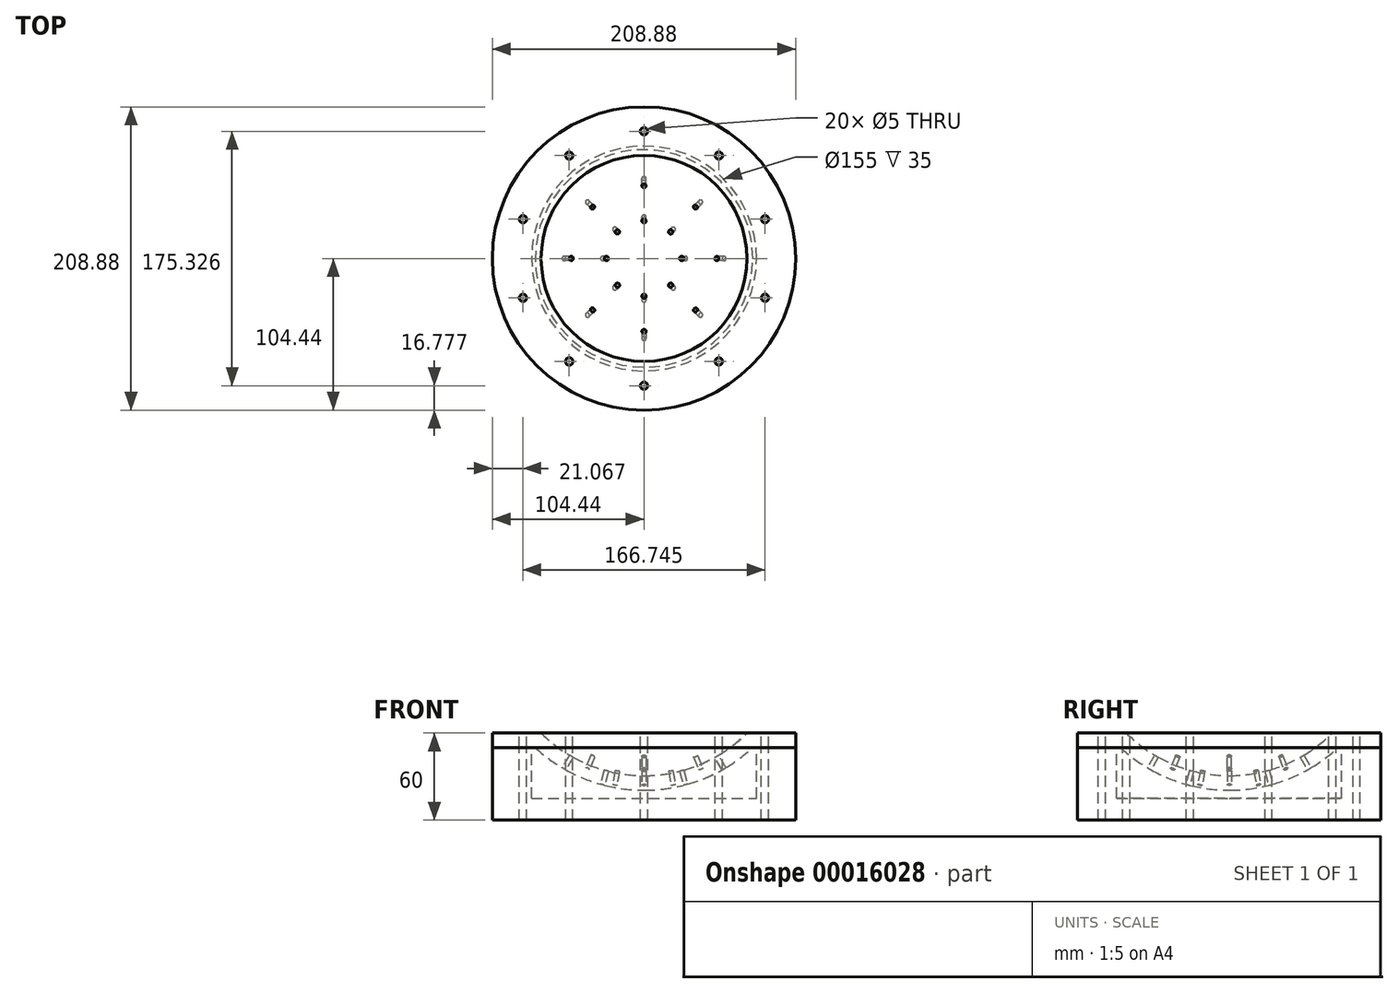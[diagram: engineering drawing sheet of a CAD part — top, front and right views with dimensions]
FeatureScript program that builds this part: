
annotation { "Feature Type Name" : "Feature", "Feature Type Description" : "" }
export const myFeature = defineFeature(function(context is Context, id is Id, definition is map)
    precondition{}
    {
        {
            var Q0;
            Q0=qCreatedBy(makeId("Front.planeOp"),FACE);
            var sketch = newSketch(context, id + "F0", { "sketchPlane" : qUnion([Q0])});
            skArc(sketch, "E0", {"start": v(0, -100.25) * mm, "mid": v(38.36, -92.62) * mm, "end": v(70.89, -70.89) * mm});
            skArc(sketch, "E1", {"start": v(0, -110.25) * mm, "mid": v(40.23, -102.65) * mm, "end": v(74.92, -80.89) * mm});
            skLineSegment(sketch, "E2", {"start": v(0, -100.25) * mm, "end": v(0, -110.25) * mm});
            skLineSegment(sketch, "E3", {"start": v(70.89, -70.89) * mm, "end": v(84.44, -70.89) * mm});
            skLineSegment(sketch, "E4", {"start": v(84.44, -70.89) * mm, "end": v(104.44, -70.89) * mm});
            skLineSegment(sketch, "E5", {"start": v(104.44, -70.89) * mm, "end": v(104.44, -80.89) * mm});
            skLineSegment(sketch, "E6", {"start": v(104.44, -80.89) * mm, "end": v(74.92, -80.89) * mm});
            skLineSegment(sketch, "E7", {"start": v(0, 0) * mm, "end": v(0, -110.25) * mm, "construction": true});
            skLineSegment(sketch, "E8", {"start": v(0, 0) * mm, "end": v(50.13, -86.82) * mm, "construction": true});
            skLineSegment(sketch, "E9", {"start": v(0, 0) * mm, "end": v(25.95, -96.83) * mm, "construction": true});
            skSolve(sketch);
        }
        {
            var Q0;
            Q0=makeQuery(id+"F0.imprint","IMPRINT",FACE,{"disambiguationData":[TD([[makeQuery(id+"F0.imprint","IMPRINT",EDGE,{"derivedFrom":sQuery(id+"F0.wireOp",EDGE,"E0")}),-1.0]])]});
            var Q1;
            Q1=sQuery(id+"F0.wireOp",EDGE,"E7");
            revolve(context, id + "F1", {"entities" : qUnion([Q0]), "axis" : qUnion([Q1]), "revolveType" : RevolveType.FULL});
        }
        {
            var Q0;
            Q0=makeQuery(id+"F1.opRevolve","SWEPT_FACE",FACE,{"disambiguationData":[OSD([sQuery(id+"F0.wireOp",EDGE,"E3"),sQuery(id+"F0.wireOp",EDGE,"E4")])]});
            var sketch = newSketch(context, id + "F2", { "sketchPlane" : qUnion([Q0])});
            skCircle(sketch, "E10", {"center": v(0, 87.66) * mm, "radius": 2.5 * mm});
            skCircle(sketch, "E11.1.0", {"center": v(-51.53, 70.92) * mm, "radius": 2.5 * mm});
            skCircle(sketch, "E11.2.0", {"center": v(-83.37, 27.09) * mm, "radius": 2.5 * mm});
            skCircle(sketch, "E11.3.0", {"center": v(-83.37, -27.09) * mm, "radius": 2.5 * mm});
            skCircle(sketch, "E11.4.0", {"center": v(-51.53, -70.92) * mm, "radius": 2.5 * mm});
            skCircle(sketch, "E11.5.0", {"center": v(0, -87.66) * mm, "radius": 2.5 * mm});
            skCircle(sketch, "E11.6.0", {"center": v(51.53, -70.92) * mm, "radius": 2.5 * mm});
            skCircle(sketch, "E11.7.0", {"center": v(83.37, -27.09) * mm, "radius": 2.5 * mm});
            skCircle(sketch, "E11.8.0", {"center": v(83.37, 27.09) * mm, "radius": 2.5 * mm});
            skCircle(sketch, "E11.9.0", {"center": v(51.53, 70.92) * mm, "radius": 2.5 * mm});
            skPoint(sketch, "E11.center", {"position": v(0, 0) * mm});
            skSolve(sketch);
        }
        {
            var Q0;
            Q0 = qSketchRegion(id + "F2", true);
            extrude(context, id + "F3", {"entities" : qUnion([Q0]), "operationType" : NewBodyOperationType.REMOVE, "endBound" : BoundingType.THROUGH_ALL, "oppositeDirection" : true, "depth" : 25 * mm});
        }
        {
            var Q0;
            Q0=sQuery(id+"F0.wireOp",EDGE,"E8");
            var Q1;
            Q1=sQuery(id+"F0.wireOp",VERTEX,"E8.end");
            cPlane(context, id + "F4", {"entities" : qUnion([Q0, Q1]), "cplaneType" : CPlaneType.LINE_POINT, "offset" : 150 * mm, "width" : 150 * mm, "height" : 150 * mm});
        }
        {
            var Q0;
            Q0=sQuery(id+"F0.wireOp",EDGE,"E9");
            var Q1;
            Q1=sQuery(id+"F0.wireOp",VERTEX,"E9.end");
            cPlane(context, id + "F5", {"entities" : qUnion([Q0, Q1]), "cplaneType" : CPlaneType.LINE_POINT, "offset" : 150 * mm, "width" : 150 * mm, "height" : 150 * mm});
        }
        {
            var Q0;
            Q0=qCreatedBy(id+"F4.planeOp",FACE);
            var sketch = newSketch(context, id + "F6", { "sketchPlane" : qUnion([Q0])});
            skCircle(sketch, "E12", {"center": v(0, 0) * mm, "radius": 1.5 * mm});
            skSolve(sketch);
        }
        {
            var Q0;
            Q0=qCreatedBy(id+"F5.planeOp",FACE);
            var sketch = newSketch(context, id + "F7", { "sketchPlane" : qUnion([Q0])});
            skCircle(sketch, "E13", {"center": v(0, 0) * mm, "radius": 1.5 * mm});
            skSolve(sketch);
        }
        {
            var Q0;
            Q0=qCreatedBy(makeId("Right.planeOp"),FACE);
            var Q1;
            Q1=qCreatedBy(makeId("Front.planeOp"),FACE);
            cPlane(context, id + "F8", {"entities" : qUnion([Q0, Q1]), "cplaneType" : CPlaneType.MID_PLANE, "offset" : 150 * mm, "width" : 150 * mm, "height" : 150 * mm});
        }
        {
            var Q0;
            Q0=qCreatedBy(makeId("Front.planeOp"),FACE);
            var Q1;
            Q1=qCreatedBy(makeId("Right.planeOp"),FACE);
            cPlane(context, id + "F9", {"entities" : qUnion([Q0, Q1]), "cplaneType" : CPlaneType.MID_PLANE, "offset" : 150 * mm, "flipAlignment" : true, "width" : 150 * mm, "height" : 150 * mm});
        }
        {
            var Q0;
            Q0=qCreatedBy(id+"F8.planeOp",FACE);
            var sketch = newSketch(context, id + "F10", { "sketchPlane" : qUnion([Q0])});
            skArc(sketch, "E14", {"start": v(0, -100.25) * mm, "mid": v(38.36, -92.62) * mm, "end": v(70.89, -70.89) * mm});
            skArc(sketch, "E15", {"start": v(0, -110.25) * mm, "mid": v(40.23, -102.65) * mm, "end": v(74.92, -80.89) * mm});
            skLineSegment(sketch, "E16", {"start": v(0, -100.25) * mm, "end": v(0, -110.25) * mm});
            skLineSegment(sketch, "E17", {"start": v(70.89, -70.89) * mm, "end": v(84.44, -70.89) * mm});
            skLineSegment(sketch, "E18", {"start": v(84.44, -70.89) * mm, "end": v(104.44, -70.89) * mm});
            skLineSegment(sketch, "E19", {"start": v(104.44, -70.89) * mm, "end": v(104.44, -80.89) * mm});
            skLineSegment(sketch, "E20", {"start": v(104.44, -80.89) * mm, "end": v(74.92, -80.89) * mm});
            skLineSegment(sketch, "E21", {"start": v(0, 0) * mm, "end": v(0, -110.25) * mm, "construction": true});
            skLineSegment(sketch, "E22", {"start": v(0, 0) * mm, "end": v(50.13, -86.82) * mm, "construction": true});
            skLineSegment(sketch, "E23", {"start": v(0, 0) * mm, "end": v(25.95, -96.83) * mm, "construction": true});
            skSolve(sketch);
        }
        {
            var Q0;
            Q0=qCreatedBy(id+"F8.planeOp",FACE);
            var sketch = newSketch(context, id + "F11", { "sketchPlane" : qUnion([Q0])});
            skArc(sketch, "E24", {"start": v(0, -100.25) * mm, "mid": v(38.36, -92.62) * mm, "end": v(70.89, -70.89) * mm});
            skArc(sketch, "E25", {"start": v(0, -110.25) * mm, "mid": v(40.23, -102.65) * mm, "end": v(74.92, -80.89) * mm});
            skLineSegment(sketch, "E26", {"start": v(0, -100.25) * mm, "end": v(0, -110.25) * mm});
            skLineSegment(sketch, "E27", {"start": v(70.89, -70.89) * mm, "end": v(84.44, -70.89) * mm});
            skLineSegment(sketch, "E28", {"start": v(84.44, -70.89) * mm, "end": v(104.44, -70.89) * mm});
            skLineSegment(sketch, "E29", {"start": v(104.44, -70.89) * mm, "end": v(104.44, -80.89) * mm});
            skLineSegment(sketch, "E30", {"start": v(104.44, -80.89) * mm, "end": v(74.92, -80.89) * mm});
            skLineSegment(sketch, "E31", {"start": v(0, 0) * mm, "end": v(0, -110.25) * mm, "construction": true});
            skLineSegment(sketch, "E32", {"start": v(0, 0) * mm, "end": v(50.13, -86.82) * mm, "construction": true});
            skLineSegment(sketch, "E33", {"start": v(0, 0) * mm, "end": v(25.95, -96.83) * mm, "construction": true});
            skLineSegment(sketch, "E34.MirrorCS", {"start": v(-104.44, -70.89) * mm, "end": v(-104.44, -80.89) * mm});
            skArc(sketch, "E35.MirrorCS", {"start": v(0, -100.25) * mm, "mid": v(-38.36, -92.62) * mm, "end": v(-70.89, -70.89) * mm});
            skArc(sketch, "E36.MirrorCS", {"start": v(0, -110.25) * mm, "mid": v(-40.23, -102.65) * mm, "end": v(-74.92, -80.89) * mm});
            skLineSegment(sketch, "E37.MirrorCS", {"start": v(-70.89, -70.89) * mm, "end": v(-84.44, -70.89) * mm});
            skLineSegment(sketch, "E38.MirrorCS", {"start": v(-84.44, -70.89) * mm, "end": v(-104.44, -70.89) * mm});
            skLineSegment(sketch, "E39.MirrorCS", {"start": v(-104.44, -80.89) * mm, "end": v(-74.92, -80.89) * mm});
            skLineSegment(sketch, "E40.MirrorCS", {"start": v(0, 0) * mm, "end": v(-25.95, -96.83) * mm});
            skLineSegment(sketch, "E41.MirrorCS", {"start": v(0, 0) * mm, "end": v(-50.12, -86.82) * mm});
            skSolve(sketch);
        }
        {
            var Q0;
            Q0=qCreatedBy(makeId("Front.planeOp"),FACE);
            var sketch = newSketch(context, id + "F12", { "sketchPlane" : qUnion([Q0])});
            skArc(sketch, "E42", {"start": v(0, -100.25) * mm, "mid": v(38.36, -92.62) * mm, "end": v(70.89, -70.89) * mm});
            skArc(sketch, "E43", {"start": v(0, -110.25) * mm, "mid": v(40.23, -102.65) * mm, "end": v(74.92, -80.89) * mm});
            skLineSegment(sketch, "E44", {"start": v(0, -100.25) * mm, "end": v(0, -110.25) * mm});
            skLineSegment(sketch, "E45", {"start": v(70.89, -70.89) * mm, "end": v(84.44, -70.89) * mm});
            skLineSegment(sketch, "E46", {"start": v(84.44, -70.89) * mm, "end": v(104.44, -70.89) * mm});
            skLineSegment(sketch, "E47", {"start": v(104.44, -70.89) * mm, "end": v(104.44, -80.89) * mm});
            skLineSegment(sketch, "E48", {"start": v(104.44, -80.89) * mm, "end": v(74.92, -80.89) * mm});
            skLineSegment(sketch, "E49", {"start": v(0, 0) * mm, "end": v(0, -110.25) * mm, "construction": true});
            skLineSegment(sketch, "E50", {"start": v(0, 0) * mm, "end": v(50.13, -86.82) * mm, "construction": true});
            skLineSegment(sketch, "E51", {"start": v(0, 0) * mm, "end": v(25.95, -96.83) * mm, "construction": true});
            skLineSegment(sketch, "E52.MirrorCS", {"start": v(-70.89, -70.89) * mm, "end": v(-84.44, -70.89) * mm});
            skLineSegment(sketch, "E53.MirrorCS", {"start": v(0, 0) * mm, "end": v(-25.95, -96.83) * mm});
            skArc(sketch, "E54.MirrorCS", {"start": v(0, -100.25) * mm, "mid": v(-38.36, -92.62) * mm, "end": v(-70.89, -70.89) * mm});
            skArc(sketch, "E55.MirrorCS", {"start": v(0, -110.25) * mm, "mid": v(-40.23, -102.65) * mm, "end": v(-74.92, -80.89) * mm});
            skLineSegment(sketch, "E56.MirrorCS", {"start": v(-84.44, -70.89) * mm, "end": v(-104.44, -70.89) * mm});
            skLineSegment(sketch, "E57.MirrorCS", {"start": v(-104.44, -70.89) * mm, "end": v(-104.44, -80.89) * mm});
            skLineSegment(sketch, "E58.MirrorCS", {"start": v(-104.44, -80.89) * mm, "end": v(-74.92, -80.89) * mm});
            skLineSegment(sketch, "E59.MirrorCS", {"start": v(0, 0) * mm, "end": v(-50.12, -86.82) * mm});
            skSolve(sketch);
        }
        {
            var Q0;
            Q0=qCreatedBy(makeId("Right.planeOp"),FACE);
            var sketch = newSketch(context, id + "F13", { "sketchPlane" : qUnion([Q0])});
            skArc(sketch, "E60", {"start": v(0, -100.25) * mm, "mid": v(38.36, -92.62) * mm, "end": v(70.89, -70.89) * mm});
            skArc(sketch, "E61", {"start": v(0, -110.25) * mm, "mid": v(40.23, -102.65) * mm, "end": v(74.92, -80.89) * mm});
            skLineSegment(sketch, "E62", {"start": v(0, -100.25) * mm, "end": v(0, -110.25) * mm});
            skLineSegment(sketch, "E63", {"start": v(70.89, -70.89) * mm, "end": v(84.44, -70.89) * mm});
            skLineSegment(sketch, "E64", {"start": v(84.44, -70.89) * mm, "end": v(104.44, -70.89) * mm});
            skLineSegment(sketch, "E65", {"start": v(104.44, -70.89) * mm, "end": v(104.44, -80.89) * mm});
            skLineSegment(sketch, "E66", {"start": v(104.44, -80.89) * mm, "end": v(74.92, -80.89) * mm});
            skLineSegment(sketch, "E67", {"start": v(0, 0) * mm, "end": v(0, -110.25) * mm, "construction": true});
            skLineSegment(sketch, "E68", {"start": v(0, 0) * mm, "end": v(50.13, -86.82) * mm, "construction": true});
            skLineSegment(sketch, "E69", {"start": v(0, 0) * mm, "end": v(25.95, -96.83) * mm, "construction": true});
            skArc(sketch, "E70.MirrorCS", {"start": v(0, -100.25) * mm, "mid": v(-38.36, -92.62) * mm, "end": v(-70.89, -70.89) * mm});
            skArc(sketch, "E71.MirrorCS", {"start": v(0, -110.25) * mm, "mid": v(-40.23, -102.65) * mm, "end": v(-74.92, -80.89) * mm});
            skLineSegment(sketch, "E72.MirrorCS", {"start": v(-70.89, -70.89) * mm, "end": v(-84.44, -70.89) * mm});
            skLineSegment(sketch, "E73.MirrorCS", {"start": v(-84.44, -70.89) * mm, "end": v(-104.44, -70.89) * mm});
            skLineSegment(sketch, "E74.MirrorCS", {"start": v(-104.44, -70.89) * mm, "end": v(-104.44, -80.89) * mm});
            skLineSegment(sketch, "E75.MirrorCS", {"start": v(-104.44, -80.89) * mm, "end": v(-74.92, -80.89) * mm});
            skLineSegment(sketch, "E76.MirrorCS", {"start": v(0, 0) * mm, "end": v(-25.95, -96.83) * mm});
            skLineSegment(sketch, "E77.MirrorCS", {"start": v(0, 0) * mm, "end": v(-50.12, -86.82) * mm});
            skSolve(sketch);
        }
        {
            var Q0;
            Q0=qCreatedBy(id+"F9.planeOp",FACE);
            var sketch = newSketch(context, id + "F14", { "sketchPlane" : qUnion([Q0])});
            skArc(sketch, "E78", {"start": v(0, -100.25) * mm, "mid": v(38.36, -92.62) * mm, "end": v(70.89, -70.89) * mm});
            skArc(sketch, "E79", {"start": v(0, -110.25) * mm, "mid": v(40.23, -102.65) * mm, "end": v(74.92, -80.89) * mm});
            skLineSegment(sketch, "E80", {"start": v(0, -100.25) * mm, "end": v(0, -110.25) * mm});
            skLineSegment(sketch, "E81", {"start": v(70.89, -70.89) * mm, "end": v(84.44, -70.89) * mm});
            skLineSegment(sketch, "E82", {"start": v(84.44, -70.89) * mm, "end": v(104.44, -70.89) * mm});
            skLineSegment(sketch, "E83", {"start": v(104.44, -70.89) * mm, "end": v(104.44, -80.89) * mm});
            skLineSegment(sketch, "E84", {"start": v(104.44, -80.89) * mm, "end": v(74.92, -80.89) * mm});
            skLineSegment(sketch, "E85", {"start": v(0, 0) * mm, "end": v(0, -110.25) * mm, "construction": true});
            skLineSegment(sketch, "E86", {"start": v(0, 0) * mm, "end": v(50.13, -86.82) * mm, "construction": true});
            skLineSegment(sketch, "E87", {"start": v(0, 0) * mm, "end": v(25.95, -96.83) * mm, "construction": true});
            skLineSegment(sketch, "E88.MirrorCS", {"start": v(-70.89, -70.89) * mm, "end": v(-84.44, -70.89) * mm});
            skArc(sketch, "E89.MirrorCS", {"start": v(0, -100.25) * mm, "mid": v(-38.36, -92.62) * mm, "end": v(-70.89, -70.89) * mm});
            skArc(sketch, "E90.MirrorCS", {"start": v(0, -110.25) * mm, "mid": v(-40.23, -102.65) * mm, "end": v(-74.92, -80.89) * mm});
            skLineSegment(sketch, "E91.MirrorCS", {"start": v(-84.44, -70.89) * mm, "end": v(-104.44, -70.89) * mm});
            skLineSegment(sketch, "E92.MirrorCS", {"start": v(-104.44, -70.89) * mm, "end": v(-104.44, -80.89) * mm});
            skLineSegment(sketch, "E93.MirrorCS", {"start": v(-104.44, -80.89) * mm, "end": v(-74.92, -80.89) * mm});
            skLineSegment(sketch, "E94.MirrorCS", {"start": v(0, 0) * mm, "end": v(-25.95, -96.83) * mm});
            skLineSegment(sketch, "E95.MirrorCS", {"start": v(0, 0) * mm, "end": v(-50.12, -86.82) * mm});
            skSolve(sketch);
        }
        {
            var Q0;
            Q0=sQuery(id+"F11.wireOp",EDGE,"E41.MirrorCS");
            var Q1;
            Q1=sQuery(id+"F11.wireOp",VERTEX,"E41.MirrorCS.end");
            cPlane(context, id + "F15", {"entities" : qUnion([Q0, Q1]), "cplaneType" : CPlaneType.LINE_POINT, "offset" : 150 * mm, "width" : 150 * mm, "height" : 150 * mm});
        }
        {
            var Q0;
            Q0=qCreatedBy(id+"F15.planeOp",FACE);
            var sketch = newSketch(context, id + "F16", { "sketchPlane" : qUnion([Q0])});
            skCircle(sketch, "E96", {"center": v(0, 0) * mm, "radius": 1.5 * mm});
            skSolve(sketch);
        }
        {
            var Q0;
            Q0=sQuery(id+"F11.wireOp",EDGE,"E40.MirrorCS");
            var Q1;
            Q1=sQuery(id+"F11.wireOp",VERTEX,"E40.MirrorCS.end");
            cPlane(context, id + "F17", {"entities" : qUnion([Q0, Q1]), "cplaneType" : CPlaneType.LINE_POINT, "offset" : 150 * mm, "width" : 150 * mm, "height" : 150 * mm});
        }
        {
            var Q0;
            Q0=qCreatedBy(id+"F17.planeOp",FACE);
            var sketch = newSketch(context, id + "F18", { "sketchPlane" : qUnion([Q0])});
            skCircle(sketch, "E97", {"center": v(0, 0) * mm, "radius": 1.5 * mm});
            skSolve(sketch);
        }
        {
            var Q0;
            Q0=sQuery(id+"F14.wireOp",EDGE,"E87");
            var Q1;
            Q1=sQuery(id+"F14.wireOp",VERTEX,"E87.end");
            cPlane(context, id + "F19", {"entities" : qUnion([Q0, Q1]), "cplaneType" : CPlaneType.LINE_POINT, "offset" : 150 * mm, "width" : 150 * mm, "height" : 150 * mm});
        }
        {
            var Q0;
            Q0=qCreatedBy(id+"F19.planeOp",FACE);
            var sketch = newSketch(context, id + "F20", { "sketchPlane" : qUnion([Q0])});
            skCircle(sketch, "E98", {"center": v(0, 0) * mm, "radius": 1.5 * mm});
            skSolve(sketch);
        }
        {
            var Q0;
            Q0=sQuery(id+"F14.wireOp",EDGE,"E86");
            var Q1;
            Q1=sQuery(id+"F14.wireOp",VERTEX,"E86.end");
            cPlane(context, id + "F21", {"entities" : qUnion([Q0, Q1]), "cplaneType" : CPlaneType.LINE_POINT, "offset" : 150 * mm, "width" : 150 * mm, "height" : 150 * mm});
        }
        {
            var Q0;
            Q0=qCreatedBy(id+"F21.planeOp",FACE);
            var sketch = newSketch(context, id + "F22", { "sketchPlane" : qUnion([Q0])});
            skCircle(sketch, "E99", {"center": v(0, 0) * mm, "radius": 1.5 * mm});
            skSolve(sketch);
        }
        {
            var Q0;
            Q0=sQuery(id+"F13.wireOp",EDGE,"E68");
            var Q1;
            Q1=sQuery(id+"F13.wireOp",VERTEX,"E68.end");
            cPlane(context, id + "F23", {"entities" : qUnion([Q0, Q1]), "cplaneType" : CPlaneType.LINE_POINT, "offset" : 150 * mm, "width" : 150 * mm, "height" : 150 * mm});
        }
        {
            var Q0;
            Q0=qCreatedBy(id+"F23.planeOp",FACE);
            var sketch = newSketch(context, id + "F24", { "sketchPlane" : qUnion([Q0])});
            skCircle(sketch, "E100", {"center": v(0, 0) * mm, "radius": 1.5 * mm});
            skSolve(sketch);
        }
        {
            var Q0;
            Q0=sQuery(id+"F13.wireOp",EDGE,"E69");
            var Q1;
            Q1=sQuery(id+"F13.wireOp",VERTEX,"E69.end");
            cPlane(context, id + "F25", {"entities" : qUnion([Q0, Q1]), "cplaneType" : CPlaneType.LINE_POINT, "offset" : 150 * mm, "width" : 150 * mm, "height" : 150 * mm});
        }
        {
            var Q0;
            Q0=qCreatedBy(id+"F25.planeOp",FACE);
            var sketch = newSketch(context, id + "F26", { "sketchPlane" : qUnion([Q0])});
            skCircle(sketch, "E101", {"center": v(0, 0) * mm, "radius": 1.5 * mm});
            skSolve(sketch);
        }
        {
            var Q0;
            Q0=sQuery(id+"F11.wireOp",EDGE,"E32");
            var Q1;
            Q1=sQuery(id+"F10.wireOp",VERTEX,"E22.end");
            cPlane(context, id + "F27", {"entities" : qUnion([Q0, Q1]), "cplaneType" : CPlaneType.LINE_POINT, "offset" : 150 * mm, "width" : 150 * mm, "height" : 150 * mm});
        }
        {
            var Q0;
            Q0=qCreatedBy(id+"F27.planeOp",FACE);
            var sketch = newSketch(context, id + "F28", { "sketchPlane" : qUnion([Q0])});
            skCircle(sketch, "E102", {"center": v(0, 0) * mm, "radius": 1.5 * mm});
            skSolve(sketch);
        }
        {
            var Q0;
            Q0=sQuery(id+"F11.wireOp",EDGE,"E33");
            var Q1;
            Q1=sQuery(id+"F10.wireOp",VERTEX,"E23.end");
            cPlane(context, id + "F29", {"entities" : qUnion([Q0, Q1]), "cplaneType" : CPlaneType.LINE_POINT, "offset" : 150 * mm, "width" : 150 * mm, "height" : 150 * mm});
        }
        {
            var Q0;
            Q0=qCreatedBy(id+"F29.planeOp",FACE);
            var sketch = newSketch(context, id + "F30", { "sketchPlane" : qUnion([Q0])});
            skCircle(sketch, "E103", {"center": v(0, 0) * mm, "radius": 1.5 * mm});
            skSolve(sketch);
        }
        {
            var Q0;
            Q0=sQuery(id+"F12.wireOp",EDGE,"E59.MirrorCS");
            var Q1;
            Q1=sQuery(id+"F12.wireOp",VERTEX,"E59.MirrorCS.end");
            cPlane(context, id + "F31", {"entities" : qUnion([Q0, Q1]), "cplaneType" : CPlaneType.LINE_POINT, "offset" : 150 * mm, "width" : 150 * mm, "height" : 150 * mm});
        }
        {
            var Q0;
            Q0=qCreatedBy(id+"F31.planeOp",FACE);
            var sketch = newSketch(context, id + "F32", { "sketchPlane" : qUnion([Q0])});
            skCircle(sketch, "E104", {"center": v(0, 0) * mm, "radius": 1.5 * mm});
            skSolve(sketch);
        }
        {
            var Q0;
            Q0=sQuery(id+"F12.wireOp",EDGE,"E53.MirrorCS");
            var Q1;
            Q1=sQuery(id+"F12.wireOp",VERTEX,"E53.MirrorCS.end");
            cPlane(context, id + "F33", {"entities" : qUnion([Q0, Q1]), "cplaneType" : CPlaneType.LINE_POINT, "offset" : 150 * mm, "width" : 150 * mm, "height" : 150 * mm});
        }
        {
            var Q0;
            Q0=qCreatedBy(id+"F33.planeOp",FACE);
            var sketch = newSketch(context, id + "F34", { "sketchPlane" : qUnion([Q0])});
            skCircle(sketch, "E105", {"center": v(0, 0) * mm, "radius": 1.5 * mm});
            skSolve(sketch);
        }
        {
            var Q0;
            Q0=sQuery(id+"F14.wireOp",EDGE,"E94.MirrorCS");
            var Q1;
            Q1=sQuery(id+"F14.wireOp",VERTEX,"E94.MirrorCS.end");
            cPlane(context, id + "F35", {"entities" : qUnion([Q0, Q1]), "cplaneType" : CPlaneType.LINE_POINT, "offset" : 150 * mm, "width" : 150 * mm, "height" : 150 * mm});
        }
        {
            var Q0;
            Q0=qCreatedBy(id+"F35.planeOp",FACE);
            var sketch = newSketch(context, id + "F36", { "sketchPlane" : qUnion([Q0])});
            skCircle(sketch, "E106", {"center": v(0, 0) * mm, "radius": 1.5 * mm});
            skSolve(sketch);
        }
        {
            var Q0;
            Q0=sQuery(id+"F14.wireOp",EDGE,"E95.MirrorCS");
            var Q1;
            Q1=sQuery(id+"F14.wireOp",VERTEX,"E95.MirrorCS.end");
            cPlane(context, id + "F37", {"entities" : qUnion([Q0, Q1]), "cplaneType" : CPlaneType.LINE_POINT, "offset" : 150 * mm, "width" : 150 * mm, "height" : 150 * mm});
        }
        {
            var Q0;
            Q0=qCreatedBy(id+"F37.planeOp",FACE);
            var sketch = newSketch(context, id + "F38", { "sketchPlane" : qUnion([Q0])});
            skCircle(sketch, "E107", {"center": v(0, 0) * mm, "radius": 1.5 * mm});
            skSolve(sketch);
        }
        {
            var Q0;
            Q0=sQuery(id+"F13.wireOp",EDGE,"E76.MirrorCS");
            var Q1;
            Q1=sQuery(id+"F13.wireOp",VERTEX,"E76.MirrorCS.end");
            cPlane(context, id + "F39", {"entities" : qUnion([Q0, Q1]), "cplaneType" : CPlaneType.LINE_POINT, "offset" : 150 * mm, "width" : 150 * mm, "height" : 150 * mm});
        }
        {
            var Q0;
            Q0=qCreatedBy(id+"F39.planeOp",FACE);
            var sketch = newSketch(context, id + "F40", { "sketchPlane" : qUnion([Q0])});
            skCircle(sketch, "E108", {"center": v(0, 0) * mm, "radius": 1.5 * mm});
            skSolve(sketch);
        }
        {
            var Q0;
            Q0=sQuery(id+"F13.wireOp",EDGE,"E77.MirrorCS");
            var Q1;
            Q1=sQuery(id+"F13.wireOp",VERTEX,"E77.MirrorCS.end");
            cPlane(context, id + "F41", {"entities" : qUnion([Q0, Q1]), "cplaneType" : CPlaneType.LINE_POINT, "offset" : 150 * mm, "width" : 150 * mm, "height" : 150 * mm});
        }
        {
            var Q0;
            Q0=qCreatedBy(id+"F41.planeOp",FACE);
            var sketch = newSketch(context, id + "F42", { "sketchPlane" : qUnion([Q0])});
            skCircle(sketch, "E109", {"center": v(0, 0) * mm, "radius": 1.5 * mm});
            skSolve(sketch);
        }
        {
            var Q0;
            Q0=makeQuery(id+"F6.imprint","IMPRINT",FACE,{"disambiguationData":[TD([[makeQuery(id+"F6.imprint","IMPRINT",EDGE,{"derivedFrom":sQuery(id+"F6.wireOp",EDGE,"E12")}),1.0]])]});
            extrude(context, id + "F43", {"entities" : qUnion([Q0]), "operationType" : NewBodyOperationType.REMOVE, "depth" : 25 * mm, "symmetric" : true});
        }
        {
            var Q0;
            Q0=makeQuery(id+"F22.imprint","IMPRINT",FACE,{"disambiguationData":[TD([[makeQuery(id+"F22.imprint","IMPRINT",EDGE,{"derivedFrom":sQuery(id+"F22.wireOp",EDGE,"E99")}),1.0]])]});
            extrude(context, id + "F44", {"entities" : qUnion([Q0]), "operationType" : NewBodyOperationType.REMOVE, "oppositeDirection" : true, "depth" : 25 * mm, "symmetric" : true});
        }
        {
            var Q0;
            Q0 = qSketchRegion(id + "F7", true);
            extrude(context, id + "F45", {"entities" : qUnion([Q0]), "operationType" : NewBodyOperationType.REMOVE, "oppositeDirection" : true, "depth" : 25 * mm, "symmetric" : true});
        }
        {
            var Q0;
            Q0 = qSketchRegion(id + "F26", true);
            extrude(context, id + "F46", {"entities" : qUnion([Q0]), "operationType" : NewBodyOperationType.REMOVE, "oppositeDirection" : true, "depth" : 25 * mm, "symmetric" : true});
        }
        {
            var Q0;
            Q0 = qSketchRegion(id + "F20", true);
            extrude(context, id + "F47", {"entities" : qUnion([Q0]), "operationType" : NewBodyOperationType.REMOVE, "oppositeDirection" : true, "depth" : 25 * mm, "symmetric" : true});
        }
        {
            var Q0;
            Q0 = qSketchRegion(id + "F34", true);
            extrude(context, id + "F48", {"entities" : qUnion([Q0]), "operationType" : NewBodyOperationType.REMOVE, "oppositeDirection" : true, "depth" : 25 * mm, "symmetric" : true});
        }
        {
            var Q0;
            Q0 = qSketchRegion(id + "F40", true);
            extrude(context, id + "F49", {"entities" : qUnion([Q0]), "operationType" : NewBodyOperationType.REMOVE, "oppositeDirection" : true, "depth" : 25 * mm, "symmetric" : true});
        }
        {
            var Q0;
            Q0=makeQuery(id+"F30.imprint","IMPRINT",FACE,{"disambiguationData":[TD([[makeQuery(id+"F30.imprint","IMPRINT",EDGE,{"derivedFrom":sQuery(id+"F30.wireOp",EDGE,"E103")}),1.0]])]});
            extrude(context, id + "F50", {"entities" : qUnion([Q0]), "operationType" : NewBodyOperationType.REMOVE, "oppositeDirection" : true, "depth" : 25 * mm, "symmetric" : true});
        }
        {
            var Q0;
            Q0 = qSketchRegion(id + "F38", true);
            extrude(context, id + "F51", {"entities" : qUnion([Q0]), "operationType" : NewBodyOperationType.REMOVE, "oppositeDirection" : true, "depth" : 25 * mm, "symmetric" : true});
        }
        {
            var Q0;
            Q0 = qSketchRegion(id + "F36", true);
            extrude(context, id + "F52", {"entities" : qUnion([Q0]), "operationType" : NewBodyOperationType.REMOVE, "oppositeDirection" : true, "depth" : 25 * mm, "symmetric" : true});
        }
        {
            var Q0;
            Q0 = qSketchRegion(id + "F32", true);
            extrude(context, id + "F53", {"entities" : qUnion([Q0]), "operationType" : NewBodyOperationType.REMOVE, "oppositeDirection" : true, "depth" : 25 * mm, "symmetric" : true});
        }
        {
            var Q0;
            Q0 = qSketchRegion(id + "F28", true);
            extrude(context, id + "F54", {"entities" : qUnion([Q0]), "operationType" : NewBodyOperationType.REMOVE, "oppositeDirection" : true, "depth" : 25 * mm, "symmetric" : true});
        }
        {
            var Q0;
            Q0 = qSketchRegion(id + "F24", true);
            extrude(context, id + "F55", {"entities" : qUnion([Q0]), "operationType" : NewBodyOperationType.REMOVE, "oppositeDirection" : true, "depth" : 25 * mm, "symmetric" : true});
        }
        {
            var Q0;
            Q0 = qSketchRegion(id + "F18", true);
            extrude(context, id + "F56", {"entities" : qUnion([Q0]), "operationType" : NewBodyOperationType.REMOVE, "oppositeDirection" : true, "depth" : 25 * mm, "symmetric" : true});
        }
        {
            var Q0;
            Q0 = qSketchRegion(id + "F16", true);
            extrude(context, id + "F57", {"entities" : qUnion([Q0]), "operationType" : NewBodyOperationType.REMOVE, "oppositeDirection" : true, "depth" : 25 * mm, "symmetric" : true});
        }
        {
            var Q0;
            Q0 = qSketchRegion(id + "F42", true);
            extrude(context, id + "F58", {"entities" : qUnion([Q0]), "operationType" : NewBodyOperationType.REMOVE, "oppositeDirection" : true, "depth" : 25 * mm, "symmetric" : true});
        }
        {
            var Q0;
            Q0=makeQuery(id+"F1.opRevolve","SWEPT_FACE",FACE,{"disambiguationData":[OSD([sQuery(id+"F0.wireOp",EDGE,"E6")])]});
            var sketch = newSketch(context, id + "F59", { "sketchPlane" : qUnion([Q0])});
            skCircle(sketch, "E110", {"center": v(0, 0) * mm, "radius": 105 * mm});
            skCircle(sketch, "E111", {"center": v(0, 0) * mm, "radius": 77.5 * mm});
            skSolve(sketch);
        }
        {
            var Q0;
            Q0=makeQuery(id+"F59.imprint","IMPRINT",FACE,{"disambiguationData":[TD([[makeQuery(id+"F59.imprint","IMPRINT",EDGE,{"derivedFrom":sQuery(id+"F59.wireOp",EDGE,"E111")}),-1.0]])]});
            extrude(context, id + "F60", {"entities" : qUnion([Q0]), "depth" : 50 * mm});
        }
        {
            var Q0;
            Q0=makeQuery(id+"F60.opExtrude","CAP_FACE",FACE,{"disambiguationData":[OSD([sQuery(id+"F0.wireOp",EDGE,"E5"),sQuery(id+"F0.wireOp",EDGE,"E6"),sQuery(id+"F2.wireOp",EDGE,"E10"),sQuery(id+"F2.wireOp",EDGE,"E11.1.0"),sQuery(id+"F2.wireOp",EDGE,"E11.2.0"),sQuery(id+"F2.wireOp",EDGE,"E11.3.0"),sQuery(id+"F2.wireOp",EDGE,"E11.4.0"),sQuery(id+"F2.wireOp",EDGE,"E11.5.0"),sQuery(id+"F2.wireOp",EDGE,"E11.6.0"),sQuery(id+"F2.wireOp",EDGE,"E11.7.0"),sQuery(id+"F2.wireOp",EDGE,"E11.8.0"),sQuery(id+"F2.wireOp",EDGE,"E11.9.0"),sQuery(id+"F59.wireOp",EDGE,"E111")])],"isStart":false});
            var sketch = newSketch(context, id + "F61", { "sketchPlane" : qUnion([Q0])});
            skCircle(sketch, "E112", {"center": v(0, 0) * mm, "radius": 77.5 * mm});
            skSolve(sketch);
        }
        {
            var Q0;
            Q0=makeQuery(id+"F61.imprint","IMPRINT",FACE,{"disambiguationData":[TD([[makeQuery(id+"F61.imprint","IMPRINT",EDGE,{"derivedFrom":sQuery(id+"F61.wireOp",EDGE,"E112")}),1.0]])]});
            extrude(context, id + "F62", {"entities" : qUnion([Q0]), "operationType" : NewBodyOperationType.ADD, "oppositeDirection" : true, "depth" : 15 * mm});
        }
    });
